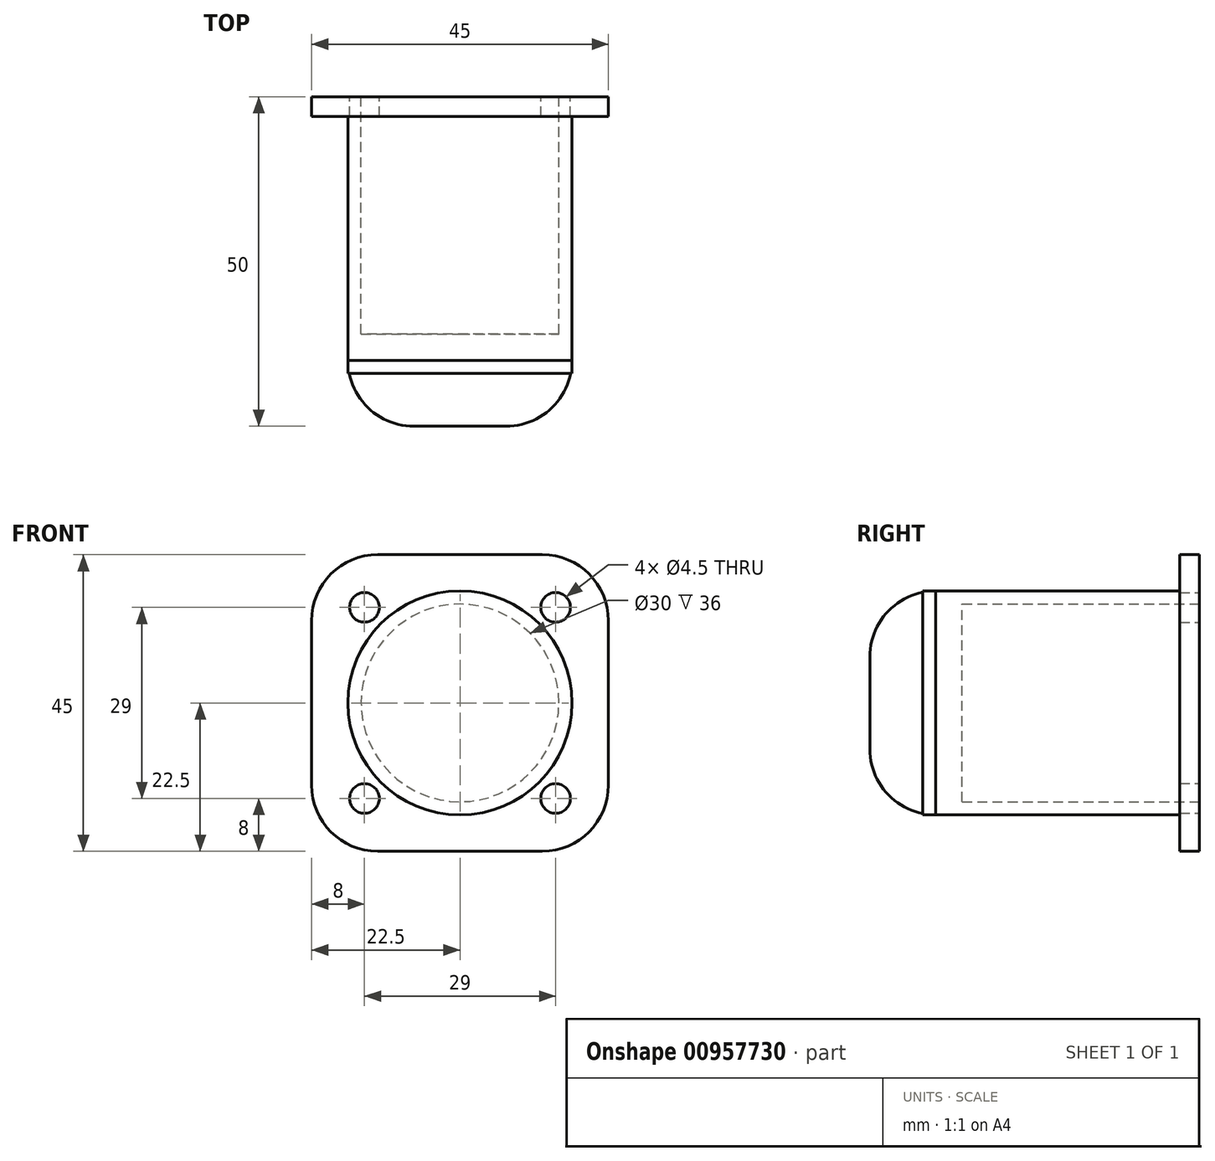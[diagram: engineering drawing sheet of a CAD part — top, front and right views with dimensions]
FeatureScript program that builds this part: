
annotation { "Feature Type Name" : "Feature", "Feature Type Description" : "" }
export const myFeature = defineFeature(function(context is Context, id is Id, definition is map)
    precondition{}
    {
        {
            var Q0;
            Q0=qCreatedBy(makeId("Front.planeOp"),FACE);
            var sketch = newSketch(context, id + "F0", { "sketchPlane" : qUnion([Q0])});
            skLineSegment(sketch, "E0.bottom", {"start": v(12.5, 22.5) * mm, "end": v(-12.5, 22.5) * mm});
            skLineSegment(sketch, "E0.top", {"start": v(12.5, -22.5) * mm, "end": v(-12.5, -22.5) * mm});
            skLineSegment(sketch, "E0.left", {"start": v(22.5, 12.5) * mm, "end": v(22.5, -12.5) * mm});
            skLineSegment(sketch, "E0.right", {"start": v(-22.5, 12.5) * mm, "end": v(-22.5, -12.5) * mm});
            skPoint(sketch, "E0.middle", {"position": v(0, 0) * mm});
            skPoint(sketch, "E1.visualSharp", {"position": v(-22.5, 22.5) * mm});
            skArc(sketch, "E1.filletArc", {"start": v(-12.5, 22.5) * mm, "mid": v(-19.57, 19.57) * mm, "end": v(-22.5, 12.5) * mm});
            skPoint(sketch, "E2.visualSharp", {"position": v(22.5, 22.5) * mm});
            skArc(sketch, "E2.filletArc", {"start": v(22.5, 12.5) * mm, "mid": v(19.57, 19.57) * mm, "end": v(12.5, 22.5) * mm});
            skPoint(sketch, "E3.visualSharp", {"position": v(22.5, -22.5) * mm});
            skArc(sketch, "E3.filletArc", {"start": v(12.5, -22.5) * mm, "mid": v(19.57, -19.57) * mm, "end": v(22.5, -12.5) * mm});
            skPoint(sketch, "E4.visualSharp", {"position": v(-22.5, -22.5) * mm});
            skArc(sketch, "E4.filletArc", {"start": v(-22.5, -12.5) * mm, "mid": v(-19.57, -19.57) * mm, "end": v(-12.5, -22.5) * mm});
            skPoint(sketch, "E5", {"position": v(-14.5, 14.5) * mm});
            skCircle(sketch, "E6", {"center": v(-14.5, 14.5) * mm, "radius": 2.25 * mm});
            skPoint(sketch, "E7.0.1.0", {"position": v(-14.5, -14.5) * mm});
            skCircle(sketch, "E7.0.1.1", {"center": v(-14.5, -14.5) * mm, "radius": 2.25 * mm});
            skPoint(sketch, "E7.1.0.0", {"position": v(14.5, 14.5) * mm});
            skCircle(sketch, "E7.1.0.1", {"center": v(14.5, 14.5) * mm, "radius": 2.25 * mm});
            skPoint(sketch, "E7.1.1.0", {"position": v(14.5, -14.5) * mm});
            skCircle(sketch, "E7.1.1.1", {"center": v(14.5, -14.5) * mm, "radius": 2.25 * mm});
            skLineSegment(sketch, "E7.direction1", {"start": v(-14.5, 14.5) * mm, "end": v(14.5, 14.5) * mm, "construction": true});
            skLineSegment(sketch, "E7.direction2", {"start": v(-14.5, 14.5) * mm, "end": v(-14.5, -14.5) * mm, "construction": true});
            skCircle(sketch, "E8", {"center": v(0, 0) * mm, "radius": 1.75 * mm});
            skCircle(sketch, "E9", {"center": v(0, 0) * mm, "radius": 15 * mm});
            skCircle(sketch, "E10", {"center": v(0, 0) * mm, "radius": 17 * mm});
            skSolve(sketch);
        }
        {
            var Q0;
            Q0=makeQuery(id+"F0.imprint","IMPRINT",FACE,{"disambiguationData":[TD([[makeQuery(id+"F0.imprint","IMPRINT",EDGE,{"derivedFrom":sQuery(id+"F0.wireOp",EDGE,"E0.bottom")}),1.0]])]});
            extrude(context, id + "F1", {"entities" : qUnion([Q0]), "depth" : 3 * mm, "offsetDistance" : 25 * mm});
        }
        {
            var Q0;
            Q0=makeQuery(id+"F0.imprint","IMPRINT",FACE,{"disambiguationData":[TD([[makeQuery(id+"F0.imprint","IMPRINT",EDGE,{"derivedFrom":sQuery(id+"F0.wireOp",EDGE,"E9")}),-1.0]])]});
            var Q1;
            Q1=makeQuery(id+"F0.imprint","IMPRINT",FACE,{"disambiguationData":[TD([[makeQuery(id+"F0.imprint","IMPRINT",EDGE,{"derivedFrom":sQuery(id+"F0.wireOp",EDGE,"E8")}),-1.0]])]});
            var Q2;
            Q2=makeQuery(id+"F0.imprint","IMPRINT",FACE,{"disambiguationData":[TD([[makeQuery(id+"F0.imprint","IMPRINT",EDGE,{"derivedFrom":sQuery(id+"F0.wireOp",EDGE,"E8")}),1.0]])]});
            extrude(context, id + "F2", {"entities" : qUnion([Q0, Q1, Q2]), "operationType" : NewBodyOperationType.ADD, "depth" : 50 * mm, "offsetDistance" : 25 * mm});
        }
        {
            var Q0;
            Q0=makeQuery(id+"F0.imprint","IMPRINT",FACE,{"disambiguationData":[TD([[makeQuery(id+"F0.imprint","IMPRINT",EDGE,{"derivedFrom":sQuery(id+"F0.wireOp",EDGE,"E8")}),-1.0]])]});
            var Q1;
            Q1=makeQuery(id+"F0.imprint","IMPRINT",FACE,{"disambiguationData":[TD([[makeQuery(id+"F0.imprint","IMPRINT",EDGE,{"derivedFrom":sQuery(id+"F0.wireOp",EDGE,"E8")}),1.0]])]});
            extrude(context, id + "F3", {"entities" : qUnion([Q0, Q1]), "operationType" : NewBodyOperationType.REMOVE, "depth" : 36 * mm, "offsetDistance" : 25 * mm});
        }
        {
            var Q0;
            Q0=makeQuery(id+"F2.opExtrude","CAP_EDGE",EDGE,{"disambiguationData":[OSD([sQuery(id+"F0.wireOp",EDGE,"E10")])],"isStart":false});
            fillet(context, id + "F4", {"entities" : qUnion([Q0]), "radius" : 10 * mm, "tangentPropagation" : true, "allowEdgeOverflow" : false});
        }
        {
            var Q0;
            Q0=qCreatedBy(makeId("Front.planeOp"),FACE);
            var sketch = newSketch(context, id + "F5", { "sketchPlane" : qUnion([Q0])});
            skCircle(sketch, "E11", {"center": v(0, 0) * mm, "radius": 17 * mm});
            skCircle(sketch, "E12", {"center": v(0, 0) * mm, "radius": 15 * mm});
            skCircle(sketch, "E13", {"center": v(0, 0) * mm, "radius": 1.75 * mm});
            skSolve(sketch);
        }
        {
            var Q0;
            Q0=makeQuery(id+"F5.imprint","IMPRINT",FACE,{"disambiguationData":[TD([[makeQuery(id+"F5.imprint","IMPRINT",EDGE,{"derivedFrom":sQuery(id+"F5.wireOp",EDGE,"E12")}),1.0]])]});
            var Q1;
            Q1=makeQuery(id+"F5.imprint","IMPRINT",FACE,{"disambiguationData":[TD([[makeQuery(id+"F5.imprint","IMPRINT",EDGE,{"derivedFrom":sQuery(id+"F5.wireOp",EDGE,"E11")}),1.0]])]});
            var Q2;
            Q2=makeQuery(id+"F5.imprint","IMPRINT",FACE,{"disambiguationData":[TD([[makeQuery(id+"F5.imprint","IMPRINT",EDGE,{"derivedFrom":sQuery(id+"F5.wireOp",EDGE,"E13")}),1.0]])]});
            extrude(context, id + "F6", {"entities" : qUnion([Q0, Q1, Q2]), "depth" : 2 * mm, "offsetDistance" : 25 * mm});
        }
        {
            var Q0;
            Q0=makeQuery(id+"F6.opExtrude","SWEPT_BODY",BODY,{"disambiguationData":[OSD([sQuery(id+"F5.wireOp",EDGE,"E11")])]});
            transform(context, id + "F7", {"entities" : qUnion([Q0]), "transformType" : TransformType.TRANSLATION_3D, "dx" : 0 * mm, "dy" : -40 * mm, "dz" : 0 * mm, "makeCopy" : false});
        }
    });
